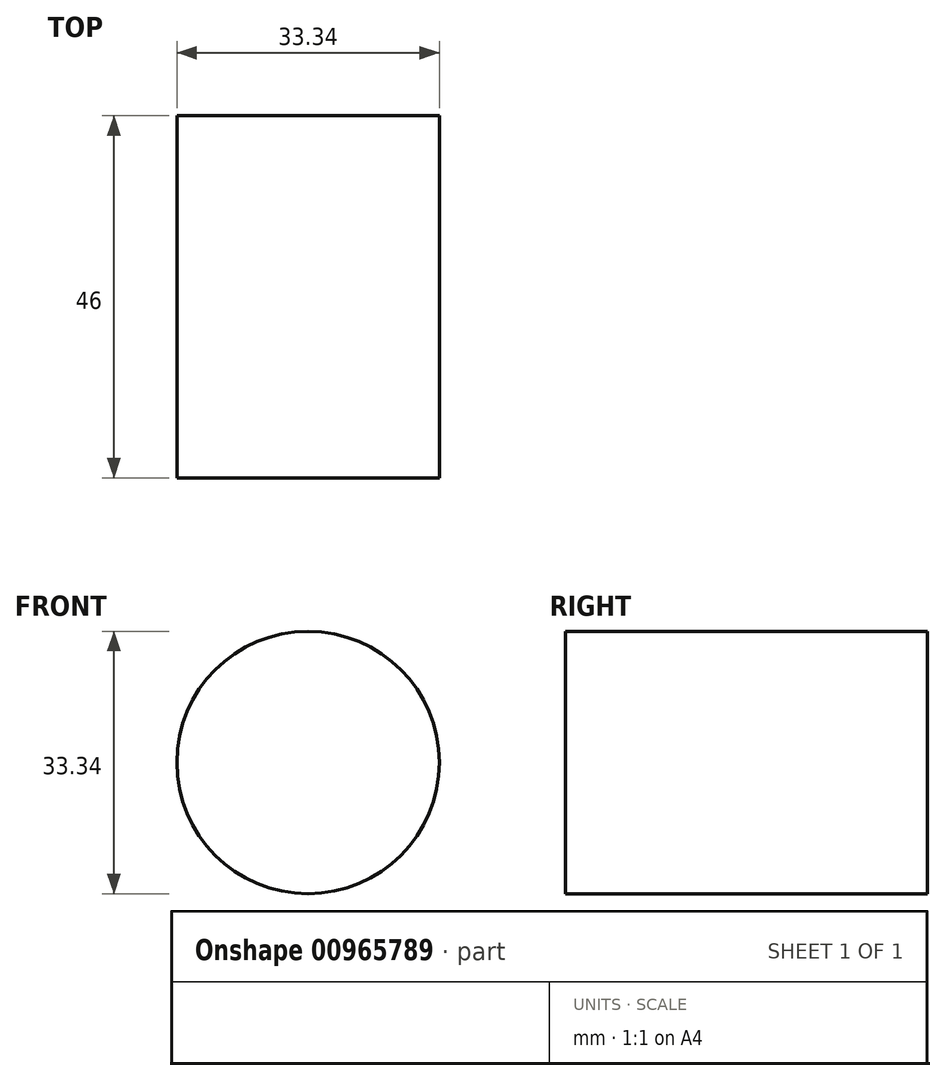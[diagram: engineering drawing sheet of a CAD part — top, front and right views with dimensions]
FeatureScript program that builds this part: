
annotation { "Feature Type Name" : "Feature", "Feature Type Description" : "" }
export const myFeature = defineFeature(function(context is Context, id is Id, definition is map)
    precondition{}
    {
        {
            var Q0;
            Q0=qCreatedBy(makeId("Front.planeOp"),FACE);
            var sketch = newSketch(context, id + "F0", { "sketchPlane" : qUnion([Q0])});
            skCircle(sketch, "E0", {"center": v(0, 0) * mm, "radius": 16.67 * mm});
            skSolve(sketch);
        }
        {
            var Q0;
            Q0=makeQuery(id+"F0.imprint","IMPRINT",FACE,{"disambiguationData":[TD([[makeQuery(id+"F0.imprint","IMPRINT",EDGE,{"derivedFrom":sQuery(id+"F0.wireOp",EDGE,"E0")}),1.0]])]});
            extrude(context, id + "F1", {"entities" : qUnion([Q0]), "depth" : 46 * mm, "offsetDistance" : 25 * mm});
        }
    });
